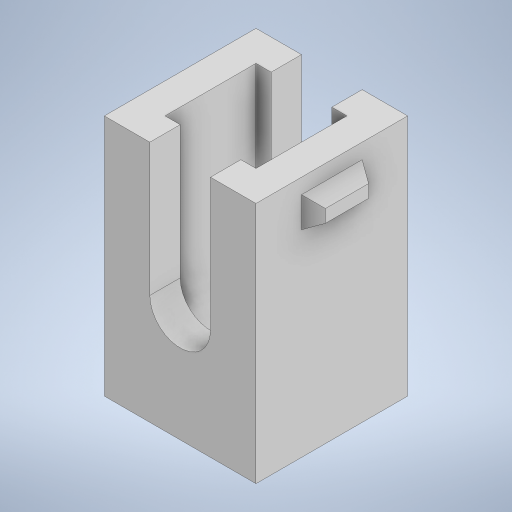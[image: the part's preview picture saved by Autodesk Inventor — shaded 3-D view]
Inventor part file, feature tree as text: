
AUTODESK INVENTOR PART (.ipt)
format: ipt  version: 2023 (Build 270158000, 158)  size: 256,512 bytes
history: native  units: in
note: dims shown in document units (in); Inventor stores cm internally (conversion verified against a paired STEP export)
features: extrude x5, sketch x5, shell x1
ambient origin geometry x8: Origin, YZ Plane, XZ Plane, XY Plane, X Axis, Y Axis, Z Axis, Center Point
bodies: Solid1 (feature_tree)
feature tree (11):
  extrude  "Extrusion1"  Depth=0.1969in
  shell  "Shell1"  Thickness=0.315in
  extrude  "Extrusion4"  Depth=0.0394in
  extrude  "Extrusion5"  Depth=0.0394in
  extrude  "Extrusion6"  Depth=0.0394in
  extrude  "Extrusion7"  Depth=0.0394in
  sketch  "Sketch1"  dims[d0=0.1969in d1=0.1969in d2=0.315in d3=0.0in]
  sketch  "Sketch9"  dims[d4=0.0394in d10=0.0394in]
  sketch  "Sketch10"  dims[d11=0.0197in d12=-0.2061in d13=0.0394in]
  sketch  "Sketch11"  dims[d14=0.0787in d15=0.0394in]
  sketch  "Sketch12"  dims[d16=0.0787in d17=0.0394in d18=0.0197in d19=-0.2061in d20=0.0787in d21=0.0in d22=0.0in d23=0.0787in d24=0.0in d25=0.0in]
